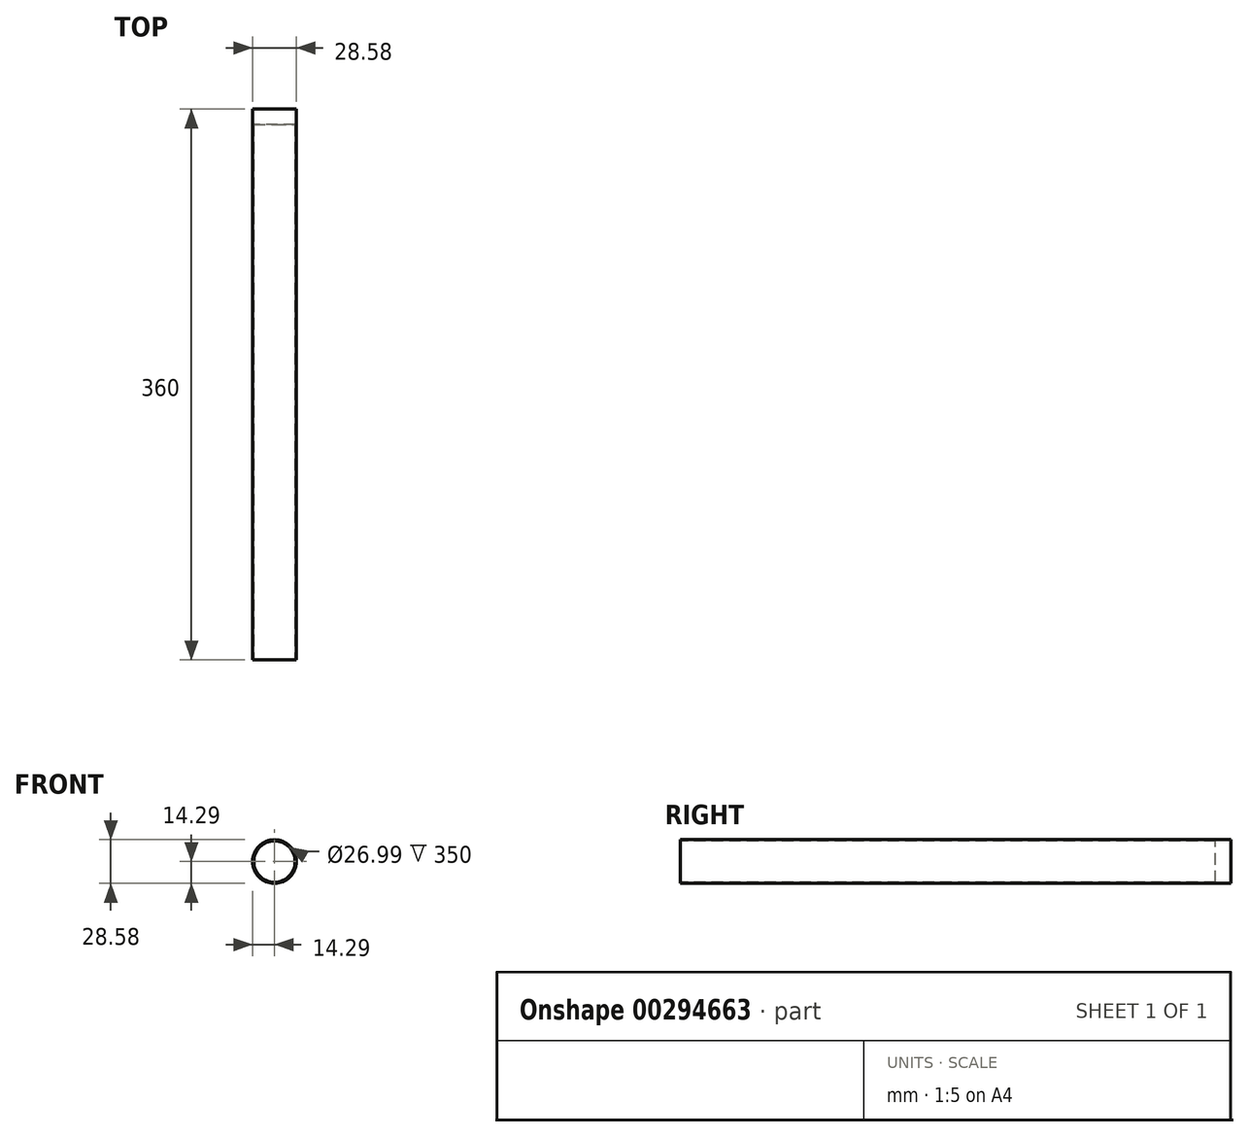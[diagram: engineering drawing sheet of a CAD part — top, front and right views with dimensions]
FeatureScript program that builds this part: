
annotation { "Feature Type Name" : "Feature", "Feature Type Description" : "" }
export const myFeature = defineFeature(function(context is Context, id is Id, definition is map)
    precondition{}
    {
        {
            var Q0;
            Q0=qCreatedBy(makeId("Front.planeOp"),FACE);
            var sketch = newSketch(context, id + "F0", { "sketchPlane" : qUnion([Q0])});
            skCircle(sketch, "E0", {"center": v(0, 0) * mm, "radius": 14.29 * mm});
            skSolve(sketch);
        }
        {
            var Q0;
            Q0 = qSketchRegion(id + "F0", true);
            extrude(context, id + "F1", {"entities" : qUnion([Q0]), "depth" : 360 * mm});
        }
        {
            var Q0;
            Q0=makeQuery(id+"F1.opExtrude","CAP_FACE",FACE,{"disambiguationData":[OSD([sQuery(id+"F0.wireOp",EDGE,"E0")])],"isStart":false});
            var sketch = newSketch(context, id + "F2", { "sketchPlane" : qUnion([Q0])});
            skCircle(sketch, "E1", {"center": v(0, 0) * mm, "radius": 13.5 * mm});
            skSolve(sketch);
        }
        {
            var Q0;
            Q0 = qSketchRegion(id + "F2", true);
            extrude(context, id + "F3", {"entities" : qUnion([Q0]), "operationType" : NewBodyOperationType.REMOVE, "oppositeDirection" : true, "depth" : 350 * mm});
        }
        {
            var Q0;
            Q0=makeQuery(id+"F1.opExtrude","CAP_FACE",FACE,{"disambiguationData":[OSD([sQuery(id+"F0.wireOp",EDGE,"E0")])],"isStart":false});
            var sketch = newSketch(context, id + "F4", { "sketchPlane" : qUnion([Q0])});
            skLineSegment(sketch, "E2", {"start": v(0, 0) * mm, "end": v(12.54, -12.54) * mm, "construction": true});
            skPoint(sketch, "E3", {"position": v(10.1, -10.1) * mm});
            skSolve(sketch);
        }
        {
            var Q0;
            Q0=qCreatedBy(makeId("Top.planeOp"),FACE);
            var Q1;
            Q1=sQuery(id+"F4.wireOp",EDGE,"E2");
            cPlane(context, id + "F5", {"entities" : qUnion([Q0, Q1]), "cplaneType" : CPlaneType.LINE_ANGLE, "offset" : 25 * mm, "angle" : 0 * degree, "width" : 150 * mm, "height" : 150 * mm});
        }
        {
            var Q0;
            Q0=qCreatedBy(id+"F5.planeOp",FACE);
            var sketch = newSketch(context, id + "F6", { "sketchPlane" : qUnion([Q0])});
            skPoint(sketch, "E4.0", {"position": v(360, -14.29) * mm});
            skLineSegment(sketch, "E5", {"start": v(360, -14.29) * mm, "end": v(372.78, -14.29) * mm, "construction": true});
            skSolve(sketch);
        }
    });
